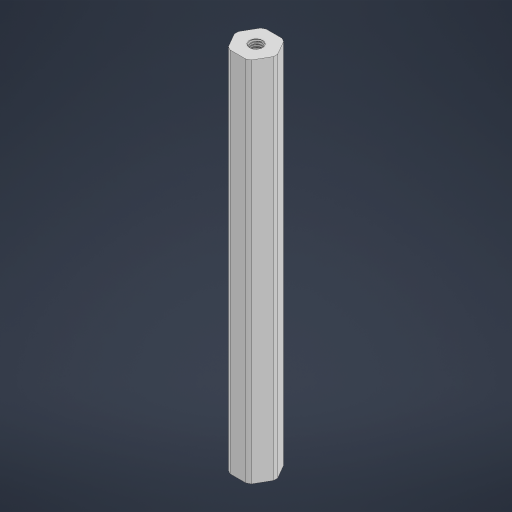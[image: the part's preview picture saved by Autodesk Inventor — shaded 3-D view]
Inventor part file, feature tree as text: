
AUTODESK INVENTOR PART (.ipt)
format: ipt  version: 2023 (Build 270158000, 158)  size: 952,320 bytes
history: native  units: in
note: dims shown in document units (in); Inventor stores cm internally (conversion verified against a paired STEP export)
features: mirror x1
ambient origin geometry x8: Origin, YZ Plane, XZ Plane, XY Plane, X Axis, Y Axis, Z Axis, Center Point
bodies: Solid1 (feature_tree)
feature tree (1):
  mirror  "Mirror2"
